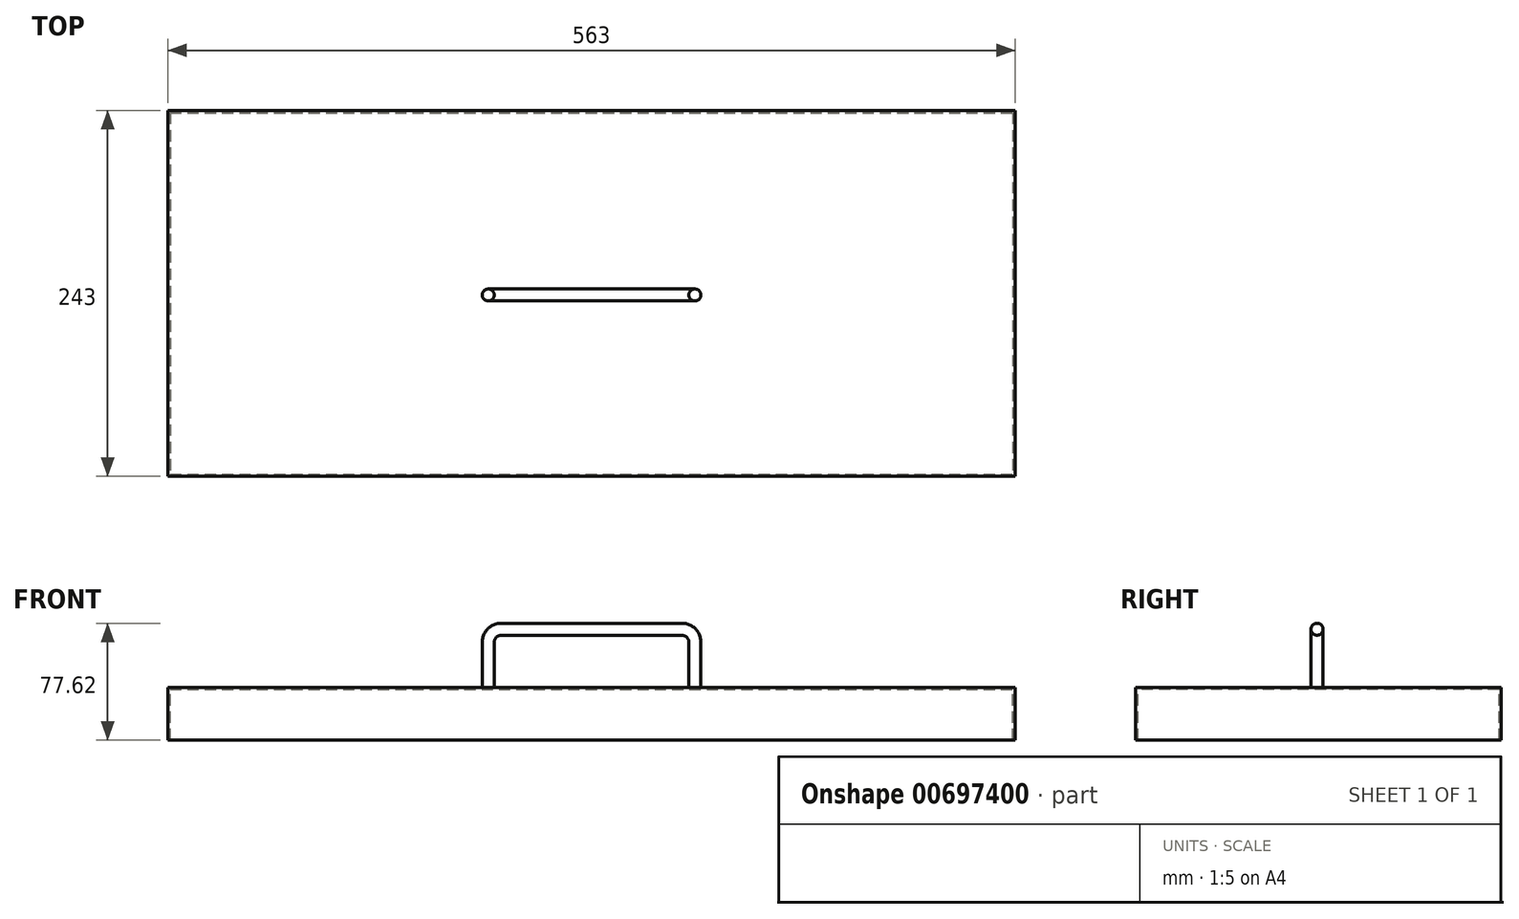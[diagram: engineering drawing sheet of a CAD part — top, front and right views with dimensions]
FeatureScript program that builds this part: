
annotation { "Feature Type Name" : "Feature", "Feature Type Description" : "" }
export const myFeature = defineFeature(function(context is Context, id is Id, definition is map)
    precondition{}
    {
        {
            var Q0;
            Q0=qCreatedBy(makeId("Top.planeOp"),FACE);
            var sketch = newSketch(context, id + "F0", { "sketchPlane" : qUnion([Q0])});
            skLineSegment(sketch, "E0.bottom", {"start": v(-97.2, 243) * mm, "end": v(465.8, 243) * mm});
            skLineSegment(sketch, "E0.top", {"start": v(-97.2, 0) * mm, "end": v(465.8, 0) * mm});
            skLineSegment(sketch, "E0.left", {"start": v(-97.2, 243) * mm, "end": v(-97.2, 0) * mm});
            skLineSegment(sketch, "E0.right", {"start": v(465.8, 243) * mm, "end": v(465.8, 0) * mm});
            skSolve(sketch);
        }
        {
            var Q0;
            Q0=makeQuery(id+"F0.imprint","IMPRINT",FACE,{"disambiguationData":[TD([[makeQuery(id+"F0.imprint","IMPRINT",EDGE,{"derivedFrom":sQuery(id+"F0.wireOp",EDGE,"E0.bottom")}),-1.0]])]});
            extrude(context, id + "F1", {"entities" : qUnion([Q0]), "oppositeDirection" : true, "depth" : 35 * mm, "offsetDistance" : 25 * mm});
        }
        {
            var Q0;
            Q0=makeQuery(id+"F1.opExtrude","CAP_FACE",FACE,{"disambiguationData":[OSD([sQuery(id+"F0.wireOp",EDGE,"E0.bottom"),sQuery(id+"F0.wireOp",EDGE,"E0.top"),sQuery(id+"F0.wireOp",EDGE,"E0.left"),sQuery(id+"F0.wireOp",EDGE,"E0.right")])],"isStart":false});
            shell(context, id + "F2", {"entities" : qUnion([Q0]), "thickness" : 1.5 * mm});
        }
        {
            var Q0;
            Q0=qCreatedBy(makeId("Front.planeOp"),FACE);
            cPlane(context, id + "F3", {"entities" : qUnion([Q0]), "cplaneType" : CPlaneType.OFFSET, "offset" : 121.5 * mm, "oppositeDirection" : true, "width" : 150 * mm, "height" : 150 * mm});
        }
        {
            var Q0;
            Q0=qCreatedBy(id+"F3.planeOp",FACE);
            var sketch = newSketch(context, id + "F4", { "sketchPlane" : qUnion([Q0])});
            skLineSegment(sketch, "E1", {"start": v(114.3, 0) * mm, "end": v(114.3, 30) * mm});
            skLineSegment(sketch, "E2", {"start": v(124.3, 40) * mm, "end": v(244.3, 40) * mm});
            skLineSegment(sketch, "E3", {"start": v(254.3, 30) * mm, "end": v(254.3, 0) * mm});
            skPoint(sketch, "E4.visualSharp", {"position": v(114.3, 40) * mm});
            skArc(sketch, "E4.filletArc", {"start": v(124.3, 40) * mm, "mid": v(117.24, 37.07) * mm, "end": v(114.3, 30) * mm});
            skPoint(sketch, "E5.visualSharp", {"position": v(254.3, 40) * mm});
            skArc(sketch, "E5.filletArc", {"start": v(254.3, 30) * mm, "mid": v(251.38, 37.07) * mm, "end": v(244.3, 40) * mm});
            skSolve(sketch);
        }
        {
            var Q0;
            Q0=makeQuery(id+"F0.imprint","IMPRINT",FACE,{"disambiguationData":[TD([[makeQuery(id+"F0.imprint","IMPRINT",EDGE,{"derivedFrom":sQuery(id+"F0.wireOp",EDGE,"E0.bottom")}),-1.0]])]});
            var sketch = newSketch(context, id + "F5", { "sketchPlane" : qUnion([Q0])});
            skCircle(sketch, "E6", {"center": v(115.69, 120.5) * mm, "radius": 4 * mm});
            skSolve(sketch);
        }
        {
            var Q0;
            Q0 = qSketchRegion(id + "F5", true);
            var Q1;
            Q1=sQuery(id+"F4.wireOp",EDGE,"E1");
            var Q2;
            Q2=sQuery(id+"F4.wireOp",EDGE,"E4.filletArc");
            var Q3;
            Q3=sQuery(id+"F4.wireOp",EDGE,"E2");
            var Q4;
            Q4=sQuery(id+"F4.wireOp",EDGE,"E5.filletArc");
            var Q5;
            Q5=sQuery(id+"F4.wireOp",EDGE,"E3");
            sweep(context, id + "F6", {"operationType" : NewBodyOperationType.ADD, "profiles" : qUnion([Q0]), "path" : qUnion([Q1, Q2, Q3, Q4, Q5])});
        }
    });
